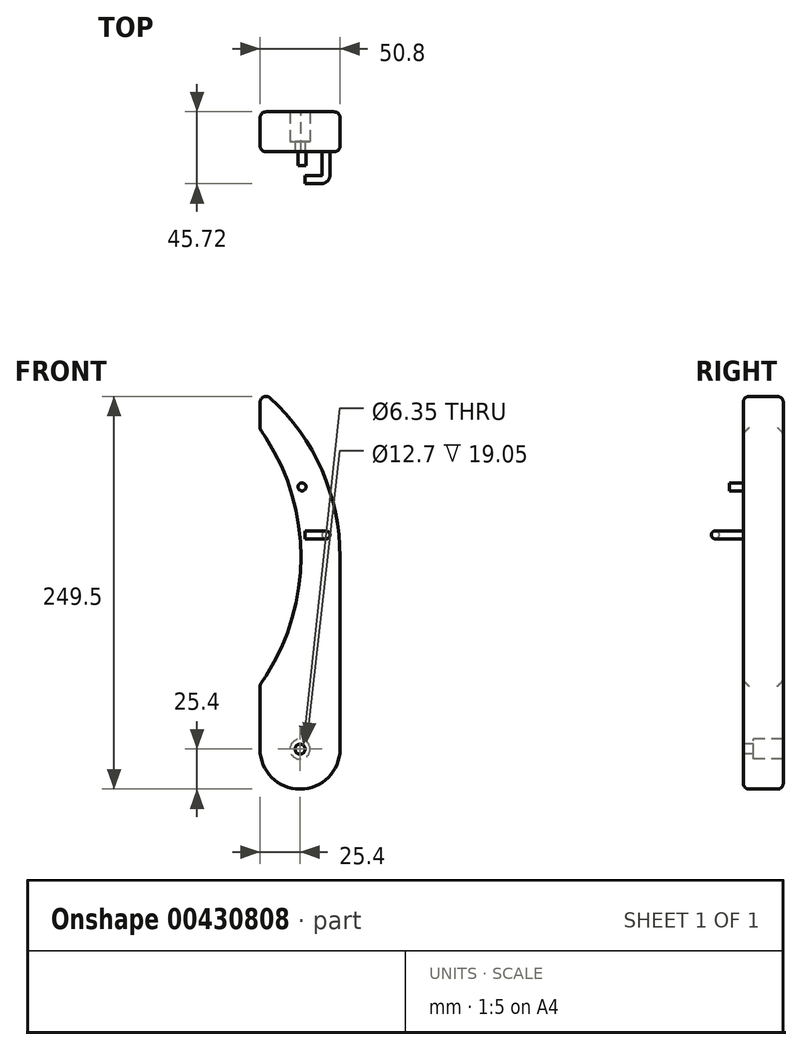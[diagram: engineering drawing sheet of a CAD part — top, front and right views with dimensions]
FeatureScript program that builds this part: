
annotation { "Feature Type Name" : "Feature", "Feature Type Description" : "" }
export const myFeature = defineFeature(function(context is Context, id is Id, definition is map)
    precondition{}
    {
        {
            var Q0;
            Q0=qCreatedBy(makeId("Front.planeOp"),FACE);
            var sketch = newSketch(context, id + "F0", { "sketchPlane" : qUnion([Q0])});
            skLineSegment(sketch, "E0.bottom", {"start": v(0, 0) * mm, "end": v(50.8, 0) * mm});
            skLineSegment(sketch, "E0.top", {"start": v(0, 254) * mm, "end": v(50.8, 254) * mm});
            skLineSegment(sketch, "E0.left", {"start": v(0, 0) * mm, "end": v(0, 254) * mm});
            skLineSegment(sketch, "E0.right", {"start": v(50.8, 0) * mm, "end": v(50.8, 254) * mm});
            skArc(sketch, "E1", {"start": v(0, 66.44) * mm, "mid": v(25.94, 147.52) * mm, "end": v(0, 228.6) * mm});
            skArc(sketch, "E2", {"start": v(0, 25.4) * mm, "mid": v(25.4, 0) * mm, "end": v(50.8, 25.4) * mm});
            skArc(sketch, "E3", {"start": v(0, 41.04) * mm, "mid": v(50.8, 147.52) * mm, "end": v(0, 254) * mm});
            skLineSegment(sketch, "E4", {"start": v(0, 25.4) * mm, "end": v(-155.84, 25.4) * mm});
            skSolve(sketch);
        }
        {
            var Q0;
            {var subQ4=sQuery(id+"F0.wireOp",EDGE,"E1");Q0=makeQuery(id+"F0.imprint","IMPRINT",FACE,{"disambiguationData":[TD([[makeQuery(id+"F0.imprint","IMPRINT",EDGE,{"derivedFrom":subQ4}),-1.0]])]});}
            var Q1;
            {var subQ0=sQuery(id+"F0.wireOp",EDGE,"E2");var subQ4=sQuery(id+"F0.wireOp",EDGE,"E0.left");var subQ5=makeQuery(id+"F0.imprint","INTERSECT",VERTEX,{"derivedFrom":[subQ4,subQ0]});Q1=makeQuery(id+"F0.imprint","IMPRINT",FACE,{"disambiguationData":[TD([[makeQuery(id+"F0.imprint","IMPRINT",EDGE,{"disambiguationData":[TD([[subQ5,-1.0]])],"derivedFrom":subQ4}),-1.0]])]});}
            extrude(context, id + "F1", {"entities" : qUnion([Q0, Q1]), "depth" : 25.4 * mm});
        }
        {
            var Q0;
            Q0=makeQuery(id+"F1.opExtrude","CAP_FACE",FACE,{"disambiguationData":[OSD([sQuery(id+"F0.wireOp",EDGE,"E0.bottom"),sQuery(id+"F0.wireOp",EDGE,"E0.top"),sQuery(id+"F0.wireOp",EDGE,"E0.left"),sQuery(id+"F0.wireOp",EDGE,"E0.right"),sQuery(id+"F0.wireOp",EDGE,"E1")])],"isStart":false});
            var sketch = newSketch(context, id + "F2", { "sketchPlane" : qUnion([Q0])});
            skCircle(sketch, "E5", {"center": v(25.4, 25.4) * mm, "radius": 3.18 * mm});
            skPoint(sketch, "E5.centerSnap0", {"position": v(25.4, 0) * mm});
            skSolve(sketch);
        }
        {
            var Q0;
            Q0=makeQuery(id+"F2.imprint","IMPRINT",FACE,{"disambiguationData":[TD([[makeQuery(id+"F2.imprint","IMPRINT",EDGE,{"derivedFrom":sQuery(id+"F2.wireOp",EDGE,"E5")}),1.0]])]});
            extrude(context, id + "F3", {"entities" : qUnion([Q0]), "operationType" : NewBodyOperationType.REMOVE, "oppositeDirection" : true, "depth" : 6.35 * mm});
        }
        {
            var Q0;
            {var subQ0=sQuery(id+"F0.wireOp",EDGE,"E0.left");Q0=makeQuery(id+"F1.opExtrude","SWEPT_FACE",FACE,{"disambiguationData":[OSD([subQ0]),TDD([makeQuery(id+"F0.imprint","IMPRINT",EDGE,{"disambiguationData":[TD([[makeQuery(id+"F0.imprint","INTERSECT",VERTEX,{"disambiguationData":[OD(1.0)],"derivedFrom":[subQ0,sQuery(id+"F0.wireOp",EDGE,"E1")]}),-1.0]])],"derivedFrom":subQ0})])]});}
            var Q1;
            {var subQ0=sQuery(id+"F0.wireOp",EDGE,"E0.left");Q1=makeQuery(id+"F1.opExtrude","SWEPT_FACE",FACE,{"disambiguationData":[OSD([subQ0]),TDD([makeQuery(id+"F0.imprint","IMPRINT",EDGE,{"disambiguationData":[TD([[makeQuery(id+"F0.imprint","INTERSECT",VERTEX,{"derivedFrom":[subQ0,sQuery(id+"F0.wireOp",EDGE,"E2")]}),-1.0]])],"derivedFrom":subQ0}),makeQuery(id+"F0.imprint","IMPRINT",EDGE,{"disambiguationData":[TD([[makeQuery(id+"F0.imprint","INTERSECT",VERTEX,{"disambiguationData":[OD(0.0)],"derivedFrom":[subQ0,sQuery(id+"F0.wireOp",EDGE,"E1")]}),1.0]])],"derivedFrom":subQ0})])]});}
            fillet(context, id + "F4", {"entities" : qUnion([Q0, Q1]), "radius" : 3.8 * mm, "tangentPropagation" : true, "allowEdgeOverflow" : false});
        }
        {
            var Q0;
            Q0=makeQuery(id+"F1.opExtrude","CAP_FACE",FACE,{"disambiguationData":[OSD([sQuery(id+"F0.wireOp",EDGE,"E0.left"),sQuery(id+"F0.wireOp",EDGE,"E0.right"),sQuery(id+"F0.wireOp",EDGE,"E1"),sQuery(id+"F0.wireOp",EDGE,"E2"),sQuery(id+"F0.wireOp",EDGE,"E3")])],"isStart":false});
            var sketch = newSketch(context, id + "F5", { "sketchPlane" : qUnion([Q0])});
            skCircle(sketch, "E6", {"center": v(26.63, 192) * mm, "radius": 2.54 * mm});
            skCircle(sketch, "E7", {"center": v(26.63, 192) * mm, "radius": 12.7 * mm, "construction": true});
            skCircle(sketch, "E8", {"center": v(26.63, 192) * mm, "radius": 6.35 * mm, "construction": true});
            skLineSegment(sketch, "E9", {"start": v(32.98, 192) * mm, "end": v(32.98, 161.5) * mm, "construction": true});
            skCircle(sketch, "E10", {"center": v(41.87, 161.5) * mm, "radius": 2.54 * mm});
            skSolve(sketch);
        }
        {
            var Q0;
            Q0=makeQuery(id+"F5.imprint","IMPRINT",FACE,{"disambiguationData":[TD([[makeQuery(id+"F5.imprint","IMPRINT",EDGE,{"derivedFrom":sQuery(id+"F5.wireOp",EDGE,"E6")}),1.0]])]});
            var Q1;
            Q1=makeQuery(id+"F5.imprint","IMPRINT",FACE,{"disambiguationData":[TD([[makeQuery(id+"F5.imprint","IMPRINT",EDGE,{"derivedFrom":sQuery(id+"F5.wireOp",EDGE,"E10")}),1.0]])]});
            extrude(context, id + "F6", {"entities" : qUnion([Q0, Q1]), "operationType" : NewBodyOperationType.ADD, "depth" : 8.9 * mm});
        }
        {
            var Q0;
            Q0=qCreatedBy(makeId("Top.planeOp"),FACE);
            cPlane(context, id + "F7", {"entities" : qUnion([Q0]), "cplaneType" : CPlaneType.OFFSET, "offset" : 161.5 * mm, "width" : 152.4 * mm, "height" : 152.4 * mm});
        }
        {
            var Q0;
            Q0=makeQuery(id+"F6.opExtrude","CAP_FACE",FACE,{"disambiguationData":[OSD([sQuery(id+"F5.wireOp",EDGE,"E10")])],"isStart":false});
            var sketch = newSketch(context, id + "F8", { "sketchPlane" : qUnion([Q0])});
            skCircle(sketch, "E11", {"center": v(41.87, 161.5) * mm, "radius": 2.54 * mm});
            skSolve(sketch);
        }
        {
            var Q0;
            Q0=qCreatedBy(id+"F7.planeOp",FACE);
            var sketch = newSketch(context, id + "F9", { "sketchPlane" : qUnion([Q0])});
            skLineSegment(sketch, "E12", {"start": v(41.87, -34.3) * mm, "end": v(41.87, -40.02) * mm});
            skLineSegment(sketch, "E13", {"start": v(38.7, -43.18) * mm, "end": v(28.54, -43.18) * mm});
            skPoint(sketch, "E14.visualSharp", {"position": v(41.87, -43.18) * mm});
            skArc(sketch, "E14.filletArc", {"start": v(38.7, -43.18) * mm, "mid": v(40.94, -42.25) * mm, "end": v(41.87, -40.02) * mm});
            skSolve(sketch);
        }
        {
            var Q0;
            Q0=makeQuery(id+"F8.imprint","IMPRINT",FACE,{"disambiguationData":[TD([[makeQuery(id+"F8.imprint","IMPRINT",EDGE,{"derivedFrom":sQuery(id+"F8.wireOp",EDGE,"E11")}),1.0]])]});
            var Q1;
            Q1=sQuery(id+"F9.wireOp",EDGE,"E12");
            var Q2;
            Q2=sQuery(id+"F9.wireOp",EDGE,"E14.filletArc");
            var Q3;
            Q3=sQuery(id+"F9.wireOp",EDGE,"E13");
            sweep(context, id + "F10", {"operationType" : NewBodyOperationType.ADD, "profiles" : qUnion([Q0]), "path" : qUnion([Q1, Q2, Q3])});
        }
        {
            var Q0;
            Q0=makeQuery(id+"F3.boolean.opBoolean","COPY",FACE,{"derivedFrom":makeQuery(id+"F3.opExtrude","CAP_FACE",FACE,{"disambiguationData":[OSD([sQuery(id+"F2.wireOp",EDGE,"E5")])],"isStart":false})});
            var sketch = newSketch(context, id + "F11", { "sketchPlane" : qUnion([Q0])});
            skCircle(sketch, "E15", {"center": v(25.4, 25.4) * mm, "radius": 6.35 * mm});
            skSolve(sketch);
        }
        {
            var Q0;
            Q0 = qSketchRegion(id + "F11", true);
            extrude(context, id + "F12", {"entities" : qUnion([Q0]), "operationType" : NewBodyOperationType.REMOVE, "oppositeDirection" : true, "depth" : 25.4 * mm});
        }
        {
            var Q0;
            Q0=qCreatedBy(makeId("Front.planeOp"),FACE);
            var sketch = newSketch(context, id + "F13", { "sketchPlane" : qUnion([Q0])});
            skCircle(sketch, "E16", {"center": v(-122.15, 147.52) * mm, "radius": 139.7 * mm});
            skSolve(sketch);
        }
    });
